# Revit family: Electronics_Messaging-Processors_Biamp_Vocia_MS-1e__
name_source: partatom
category: Communication Devices
units: mm (PartAtom-declared; Revit-internal decimal feet)

## family parameters
Cut with Voids When Loaded = No
Host = Face
Maintain Annotation Orientation = No
OmniClass Number = 23.85.10.11.11
OmniClass Title = Sound and Signal Devices
Part Type = Normal
Room Calculation Point = No
Round Connector Dimension = Use Diameter
Shared = No

## types (1)
- MS-1e
    Altitude = 0-10,000 ft (0-3000m) MSL
    Apparent Load = 300 VA
    Compliance = FCC Part 15 Class A (USA), CE marked (Europe), UL listed (USA and Canada), RoHS Directive (Europe)
    Connector Description = 100-240VAC 50/60Hz
    Default Elevation = 48 "
    Depth = 17.5 "
    Description = Vocia® MS-1e Message Processor
    Height = 1.75 "
    Housing Material = Biamp - Metal - Black
    Humidity = 5-95% non-condensing
    Manufacturer = Biamp
    Max Power Consumption = 300 W
    Model = Vocia MS-1e
    Network Connection = RJ-45 with shielded Ethernet (CAT5, CAT5e, CAT6, or CAT7)
    Number of Poles = 1
    Power Factor = 1
    Product Documentation Link = https://downloads.biamp.com
    Product Page URL = https://www.biamp.com
    Product data url = https://www.bimobject.com
    Temperature Range = 32 - 113° F (0 – 45° C)
    URL = https://www.biamp.com
    Voltage = 120 V
    Weight = 12.00 lbf
    Width = 19 "

## geometry (parser evidence)
native form markers: Sweep x2
no freeform markers — native parametric forms only
